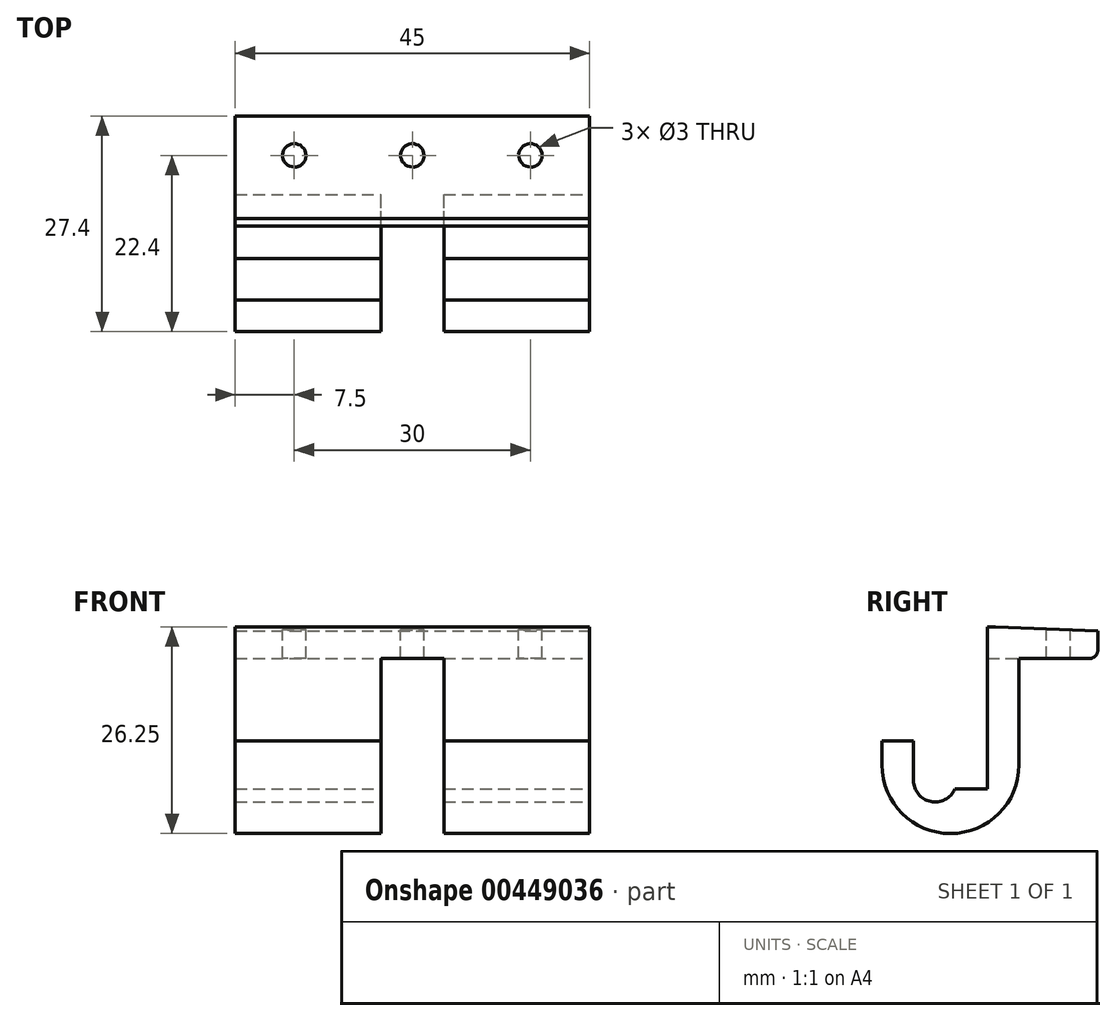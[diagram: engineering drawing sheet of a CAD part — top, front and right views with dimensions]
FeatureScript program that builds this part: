
annotation { "Feature Type Name" : "Feature", "Feature Type Description" : "" }
export const myFeature = defineFeature(function(context is Context, id is Id, definition is map)
    precondition{}
    {
        {
            var Q0;
            Q0=qCreatedBy(makeId("Front.planeOp"),FACE);
            var sketch = newSketch(context, id + "F0", { "sketchPlane" : qUnion([Q0])});
            skLineSegment(sketch, "E0.bottom", {"start": v(-22.5, 13.12) * mm, "end": v(22.5, 13.12) * mm});
            skLineSegment(sketch, "E0.top", {"start": v(-22.5, -13.12) * mm, "end": v(22.5, -13.12) * mm});
            skLineSegment(sketch, "E0.left", {"start": v(-22.5, 13.12) * mm, "end": v(-22.5, -13.12) * mm});
            skLineSegment(sketch, "E0.right", {"start": v(22.5, 13.12) * mm, "end": v(22.5, -13.12) * mm});
            skPoint(sketch, "E0.middle", {"position": v(0, 0) * mm});
            skSolve(sketch);
        }
        {
            var Q0;
            Q0=makeQuery(id+"F0.imprint","IMPRINT",FACE,{"disambiguationData":[TD([[makeQuery(id+"F0.imprint","IMPRINT",EDGE,{"derivedFrom":sQuery(id+"F0.wireOp",EDGE,"E0.bottom")}),-1.0]])]});
            extrude(context, id + "F1", {"entities" : qUnion([Q0]), "depth" : 17.4 * mm});
        }
        {
            var Q0;
            Q0=makeQuery(id+"F1.opExtrude","CAP_FACE",FACE,{"disambiguationData":[OSD([sQuery(id+"F0.wireOp",EDGE,"E0.bottom"),sQuery(id+"F0.wireOp",EDGE,"E0.top"),sQuery(id+"F0.wireOp",EDGE,"E0.left"),sQuery(id+"F0.wireOp",EDGE,"E0.right")])],"isStart":true});
            var sketch = newSketch(context, id + "F2", { "sketchPlane" : qUnion([Q0])});
            skLineSegment(sketch, "E1.bottom", {"start": v(22.5, 13.12) * mm, "end": v(-22.5, 13.12) * mm});
            skLineSegment(sketch, "E1.top", {"start": v(22.5, 9.12) * mm, "end": v(-22.5, 9.12) * mm});
            skLineSegment(sketch, "E1.left", {"start": v(22.5, 13.12) * mm, "end": v(22.5, 9.12) * mm});
            skLineSegment(sketch, "E1.right", {"start": v(-22.5, 13.12) * mm, "end": v(-22.5, 9.12) * mm});
            skSolve(sketch);
        }
        {
            var Q0;
            Q0=makeQuery(id+"F2.imprint","IMPRINT",FACE,{"disambiguationData":[TD([[makeQuery(id+"F2.imprint","IMPRINT",EDGE,{"derivedFrom":sQuery(id+"F2.wireOp",EDGE,"E1.bottom")}),1.0]])]});
            extrude(context, id + "F3", {"entities" : qUnion([Q0]), "operationType" : NewBodyOperationType.ADD, "depth" : 10 * mm});
        }
        {
            var Q0;
            Q0=makeQuery(id+"F3.boolean.opBoolean","MERGE",FACE,{"derivedFrom":[makeQuery(id+"F1.opExtrude","SWEPT_FACE",FACE,{"disambiguationData":[OSD([sQuery(id+"F0.wireOp",EDGE,"E0.right")])]}),makeQuery(id+"F3.opExtrude","SWEPT_FACE",FACE,{"disambiguationData":[OSD([sQuery(id+"F2.wireOp",EDGE,"E1.right")])]})]});
            var sketch = newSketch(context, id + "F4", { "sketchPlane" : qUnion([Q0])});
            skArc(sketch, "E2", {"start": v(-13.4, -6.37) * mm, "mid": v(-10.65, -9.12) * mm, "end": v(-7.9, -6.37) * mm});
            skLineSegment(sketch, "E3", {"start": v(-4, -7.47) * mm, "end": v(-4, 13.13) * mm});
            skLineSegment(sketch, "E4", {"start": v(-8.13, -7.47) * mm, "end": v(-4.5, -7.47) * mm});
            skLineSegment(sketch, "E5", {"start": v(-4.5, -7.47) * mm, "end": v(-4, -7.47) * mm});
            skLineSegment(sketch, "E6", {"start": v(-13.4, -6.37) * mm, "end": v(-13.4, -1.37) * mm});
            skLineSegment(sketch, "E7", {"start": v(-13.4, -1.37) * mm, "end": v(-17.4, -1.37) * mm});
            skSolve(sketch);
        }
        {
            var Q0;
            {var subQ0=sQuery(id+"F4.wireOp",EDGE,"aqZgDZ6p-uxGR-Qi7A-fzvt-bBAgb4r7ZHrh");var subQ1=makeQuery(id+"F1.opExtrude","CAP_EDGE",EDGE,{"disambiguationData":[OSD([sQuery(id+"F0.wireOp",EDGE,"E0.right")])],"isStart":false});var subQ2=makeQuery(id+"F4.imprint","INTERSECT",VERTEX,{"disambiguationData":[OD(0.0)],"derivedFrom":[subQ1,subQ0]});Q0=makeQuery(id+"F4.imprint","IMPRINT",FACE,{"disambiguationData":[TD([[makeQuery(id+"F4.imprint","IMPRINT",EDGE,{"disambiguationData":[TD([[subQ2,1.0]])],"derivedFrom":subQ1}),1.0]])]});}
            var Q1;
            {var subQ4=sQuery(id+"F4.wireOp",EDGE,"WoVsaCIx-hBhL-SycB-xlvc-rFWzZC1cRBzN");Q1=makeQuery(id+"F4.imprint","IMPRINT",FACE,{"disambiguationData":[TD([[makeQuery(id+"F4.imprint","IMPRINT",EDGE,{"derivedFrom":subQ4}),1.0]])]});}
            var Q2;
            {var subQ0=sQuery(id+"F4.wireOp",EDGE,"aqZgDZ6p-uxGR-Qi7A-fzvt-bBAgb4r7ZHrh");var subQ1=makeQuery(id+"F1.opExtrude","CAP_EDGE",EDGE,{"disambiguationData":[OSD([sQuery(id+"F0.wireOp",EDGE,"E0.right")])],"isStart":false});var subQ2=makeQuery(id+"F4.imprint","INTERSECT",VERTEX,{"disambiguationData":[OD(1.0)],"derivedFrom":[subQ1,subQ0]});Q2=makeQuery(id+"F4.imprint","IMPRINT",FACE,{"disambiguationData":[TD([[makeQuery(id+"F4.imprint","IMPRINT",EDGE,{"disambiguationData":[TD([[subQ2,-1.0]])],"derivedFrom":subQ1}),1.0]])]});}
            extrude(context, id + "F5", {"entities" : qUnion([Q0, Q1, Q2]), "operationType" : NewBodyOperationType.REMOVE, "oppositeDirection" : true, "depth" : 45 * mm});
        }
        {
            var Q0;
            Q0=makeQuery(id+"F3.opExtrude","SWEPT_FACE",FACE,{"disambiguationData":[OSD([sQuery(id+"F2.wireOp",EDGE,"E1.top")])]});
            var sketch = newSketch(context, id + "F6", { "sketchPlane" : qUnion([Q0])});
            skPoint(sketch, "E8", {"position": v(-15, -5) * mm});
            skPoint(sketch, "E9", {"position": v(0, -5) * mm});
            skPoint(sketch, "E10", {"position": v(15, -5) * mm});
            skSolve(sketch);
        }
        {
            var Q0;
            Q0=sQuery(id+"F6.wireOp",VERTEX,"E8");
            var Q1;
            Q1=sQuery(id+"F6.wireOp",VERTEX,"E9");
            var Q2;
            Q2=sQuery(id+"F6.wireOp",VERTEX,"E10");
            var Q3;
            Q3=makeQuery(id+"F1.opExtrude","SWEPT_BODY",BODY,{"disambiguationData":[OSD([sQuery(id+"F0.wireOp",EDGE,"E0.bottom"),sQuery(id+"F0.wireOp",EDGE,"E0.top"),sQuery(id+"F0.wireOp",EDGE,"E0.left"),sQuery(id+"F0.wireOp",EDGE,"E0.right")])]});
            hole(context, id + "F7", {"style" : HoleStyle.SIMPLE, "endStyle" : HoleEndStyle.THROUGH, "holeDiameter" : 3 * mm, "isTappedThrough" : true, "tappedDepth" : 12 * mm, "tapClearance" : 3, "startFromSketch" : true, "locations" : qUnion([Q0, Q1, Q2]), "scope" : qUnion([Q3])});
        }
        {
            var Q0;
            Q0=makeQuery(id+"F3.opExtrude","CAP_EDGE",EDGE,{"disambiguationData":[OSD([sQuery(id+"F2.wireOp",EDGE,"E1.bottom")])],"isStart":false});
            chamfer(context, id + "F8", {"entities" : qUnion([Q0]), "chamferType" : ChamferType.TWO_OFFSETS, "width1" : 13 * mm, "oppositeDirection" : true, "width2" : 0.5 * mm});
        }
        {
            var Q0;
            Q0=makeQuery(id+"F1.opExtrude","CAP_FACE",FACE,{"disambiguationData":[OSD([sQuery(id+"F0.wireOp",EDGE,"E0.bottom"),sQuery(id+"F0.wireOp",EDGE,"E0.top"),sQuery(id+"F0.wireOp",EDGE,"E0.left"),sQuery(id+"F0.wireOp",EDGE,"E0.right")])],"isStart":true});
            var sketch = newSketch(context, id + "F9", { "sketchPlane" : qUnion([Q0])});
            skLineSegment(sketch, "E11.bottom", {"start": v(-4, 9.12) * mm, "end": v(4, 9.12) * mm});
            skLineSegment(sketch, "E11.top", {"start": v(-4, -14.24) * mm, "end": v(4, -14.24) * mm});
            skLineSegment(sketch, "E11.left", {"start": v(-4, 9.12) * mm, "end": v(-4, -14.24) * mm});
            skLineSegment(sketch, "E11.right", {"start": v(4, 9.12) * mm, "end": v(4, -14.24) * mm});
            skSolve(sketch);
        }
        {
            var Q0;
            {var subQ0=sQuery(id+"F9.wireOp",EDGE,"E11.bottom");Q0=makeQuery(id+"F9.imprint","IMPRINT",FACE,{"disambiguationData":[TD([[makeQuery(id+"F9.imprint","IMPRINT",EDGE,{"derivedFrom":subQ0}),1.0]])]});}
            var Q1;
            {var subQ0=sQuery(id+"F9.wireOp",EDGE,"E11.top");Q1=makeQuery(id+"F9.imprint","IMPRINT",FACE,{"disambiguationData":[TD([[makeQuery(id+"F9.imprint","IMPRINT",EDGE,{"derivedFrom":subQ0}),1.0]])]});}
            extrude(context, id + "F10", {"entities" : qUnion([Q0, Q1]), "operationType" : NewBodyOperationType.REMOVE, "oppositeDirection" : true, "depth" : 21.5 * mm});
        }
        {
            var Q0;
            {var subQ0=sQuery(id+"F0.wireOp",EDGE,"E0.left");var subQ1=sQuery(id+"F0.wireOp",EDGE,"E0.top");Q0=makeQuery(id+"F10.boolean.opBoolean","SPLIT",EDGE,{"disambiguationData":[TD([makeQuery(id+"F1.opExtrude","SWEPT_FACE",FACE,{"disambiguationData":[OSD([subQ0])]})])],"derivedFrom":makeQuery(id+"F1.opExtrude","CAP_EDGE",EDGE,{"disambiguationData":[OSD([subQ1])],"isStart":false})});}
            var Q1;
            {var subQ0=sQuery(id+"F0.wireOp",EDGE,"E0.left");var subQ1=sQuery(id+"F0.wireOp",EDGE,"E0.top");Q1=makeQuery(id+"F10.boolean.opBoolean","SPLIT",EDGE,{"disambiguationData":[TD([makeQuery(id+"F1.opExtrude","SWEPT_FACE",FACE,{"disambiguationData":[OSD([subQ0])]})])],"derivedFrom":makeQuery(id+"F1.opExtrude","CAP_EDGE",EDGE,{"disambiguationData":[OSD([subQ1])],"isStart":true})});}
            var Q2;
            {var subQ0=sQuery(id+"F0.wireOp",EDGE,"E0.right");var subQ1=sQuery(id+"F0.wireOp",EDGE,"E0.top");Q2=makeQuery(id+"F10.boolean.opBoolean","SPLIT",EDGE,{"disambiguationData":[TD([makeQuery(id+"F1.opExtrude","SWEPT_FACE",FACE,{"disambiguationData":[OSD([subQ0])]})])],"derivedFrom":makeQuery(id+"F1.opExtrude","CAP_EDGE",EDGE,{"disambiguationData":[OSD([subQ1])],"isStart":false})});}
            var Q3;
            {var subQ0=sQuery(id+"F0.wireOp",EDGE,"E0.right");var subQ1=sQuery(id+"F0.wireOp",EDGE,"E0.top");Q3=makeQuery(id+"F10.boolean.opBoolean","SPLIT",EDGE,{"disambiguationData":[TD([makeQuery(id+"F1.opExtrude","SWEPT_FACE",FACE,{"disambiguationData":[OSD([subQ0])]})])],"derivedFrom":makeQuery(id+"F1.opExtrude","CAP_EDGE",EDGE,{"disambiguationData":[OSD([subQ1])],"isStart":true})});}
            fillet(context, id + "F11", {"entities" : qUnion([Q0, Q1, Q2, Q3]), "radius" : 8.7 * mm, "tangentPropagation" : true, "allowEdgeOverflow" : false});
        }
        {
            var Q0;
            Q0=makeQuery(id+"F3.opExtrude","CAP_EDGE",EDGE,{"disambiguationData":[OSD([sQuery(id+"F2.wireOp",EDGE,"E1.top")])],"isStart":false});
            var Q1;
            Q1=makeQuery(id+"F5.boolean.opBoolean","COPY",EDGE,{"derivedFrom":makeQuery(id+"F5.opExtrude","SWEPT_EDGE",EDGE,{"disambiguationData":[OSD([sQuery(id+"F0.wireOp",EDGE,"E0.bottom"),sQuery(id+"F0.wireOp",EDGE,"E0.right"),sQuery(id+"F2.wireOp",EDGE,"E1.bottom"),sQuery(id+"F2.wireOp",EDGE,"E1.right"),sQuery(id+"F4.wireOp",EDGE,"E3")])]})});
            fillet(context, id + "F12", {"entities" : qUnion([Q0, Q1]), "radius" : 1 * mm, "tangentPropagation" : true, "allowEdgeOverflow" : false});
        }
    });
